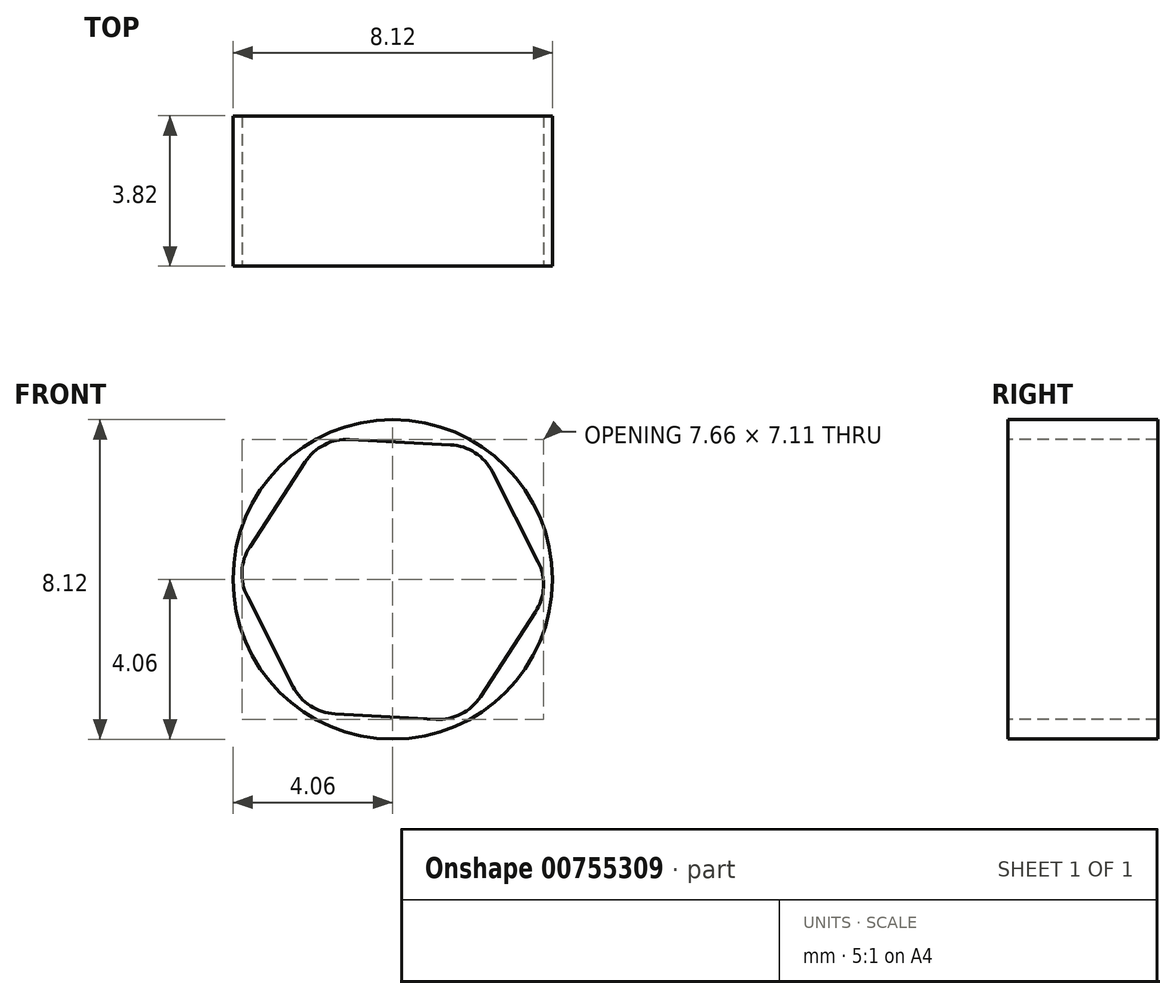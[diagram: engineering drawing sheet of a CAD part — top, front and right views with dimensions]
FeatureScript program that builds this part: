
annotation { "Feature Type Name" : "Feature", "Feature Type Description" : "" }
export const myFeature = defineFeature(function(context is Context, id is Id, definition is map)
    precondition{}
    {
        {
            var Q0;
            Q0=qCreatedBy(makeId("Front.planeOp"),FACE);
            var sketch = newSketch(context, id + "F0", { "sketchPlane" : qUnion([Q0])});
            skCircle(sketch, "E0.cCircle", {"center": v(0, 0) * mm, "radius": 3.5 * mm, "construction": true});
            skLineSegment(sketch, "E0.0", {"start": v(2.2, 3.38) * mm, "end": v(4.03, -0.21) * mm});
            skLineSegment(sketch, "E0.1", {"start": v(4.03, -0.21) * mm, "end": v(1.83, -3.6) * mm});
            skLineSegment(sketch, "E0.2", {"start": v(1.83, -3.6) * mm, "end": v(-2.2, -3.38) * mm});
            skLineSegment(sketch, "E0.3", {"start": v(-2.2, -3.38) * mm, "end": v(-4.03, 0.21) * mm});
            skLineSegment(sketch, "E0.4", {"start": v(-4.03, 0.21) * mm, "end": v(-1.83, 3.6) * mm});
            skLineSegment(sketch, "E0.5", {"start": v(-1.83, 3.6) * mm, "end": v(2.2, 3.38) * mm});
            skPoint(sketch, "E0.0.midPoint", {"position": v(3.11, 1.58) * mm});
            skCircle(sketch, "E1", {"center": v(0, 0) * mm, "radius": 4.06 * mm});
            skSolve(sketch);
        }
        {
            var Q0;
            Q0=makeQuery(id+"F0.imprint","IMPRINT",FACE,{"disambiguationData":[TD([[makeQuery(id+"F0.imprint","IMPRINT",EDGE,{"derivedFrom":sQuery(id+"F0.wireOp",EDGE,"E0.0")}),1.0]])]});
            extrude(context, id + "F1", {"entities" : qUnion([Q0]), "depth" : 3.8 * mm, "offsetDistance" : 25.4 * mm, "symmetric" : true});
        }
        {
            var Q0;
            Q0=makeQuery(id+"F1.opExtrude","SWEPT_EDGE",EDGE,{"disambiguationData":[OSD([sQuery(id+"F0.wireOp",EDGE,"E0.4"),sQuery(id+"F0.wireOp",EDGE,"E0.5")])]});
            var Q1;
            Q1=makeQuery(id+"F1.opExtrude","SWEPT_EDGE",EDGE,{"disambiguationData":[OSD([sQuery(id+"F0.wireOp",EDGE,"E0.0"),sQuery(id+"F0.wireOp",EDGE,"E0.5")])]});
            var Q2;
            Q2=makeQuery(id+"F1.opExtrude","SWEPT_EDGE",EDGE,{"disambiguationData":[OSD([sQuery(id+"F0.wireOp",EDGE,"E0.0"),sQuery(id+"F0.wireOp",EDGE,"E0.1")])]});
            var Q3;
            Q3=makeQuery(id+"F1.opExtrude","SWEPT_EDGE",EDGE,{"disambiguationData":[OSD([sQuery(id+"F0.wireOp",EDGE,"E0.3"),sQuery(id+"F0.wireOp",EDGE,"E0.4")])]});
            var Q4;
            Q4=makeQuery(id+"F1.opExtrude","SWEPT_EDGE",EDGE,{"disambiguationData":[OSD([sQuery(id+"F0.wireOp",EDGE,"E0.2"),sQuery(id+"F0.wireOp",EDGE,"E0.3")])]});
            var Q5;
            Q5=makeQuery(id+"F1.opExtrude","SWEPT_EDGE",EDGE,{"disambiguationData":[OSD([sQuery(id+"F0.wireOp",EDGE,"E0.1"),sQuery(id+"F0.wireOp",EDGE,"E0.2")])]});
            fillet(context, id + "F2", {"entities" : qUnion([Q0, Q1, Q2, Q3, Q4, Q5]), "radius" : 1.27 * mm, "tangentPropagation" : true, "allowEdgeOverflow" : false});
        }
    });
